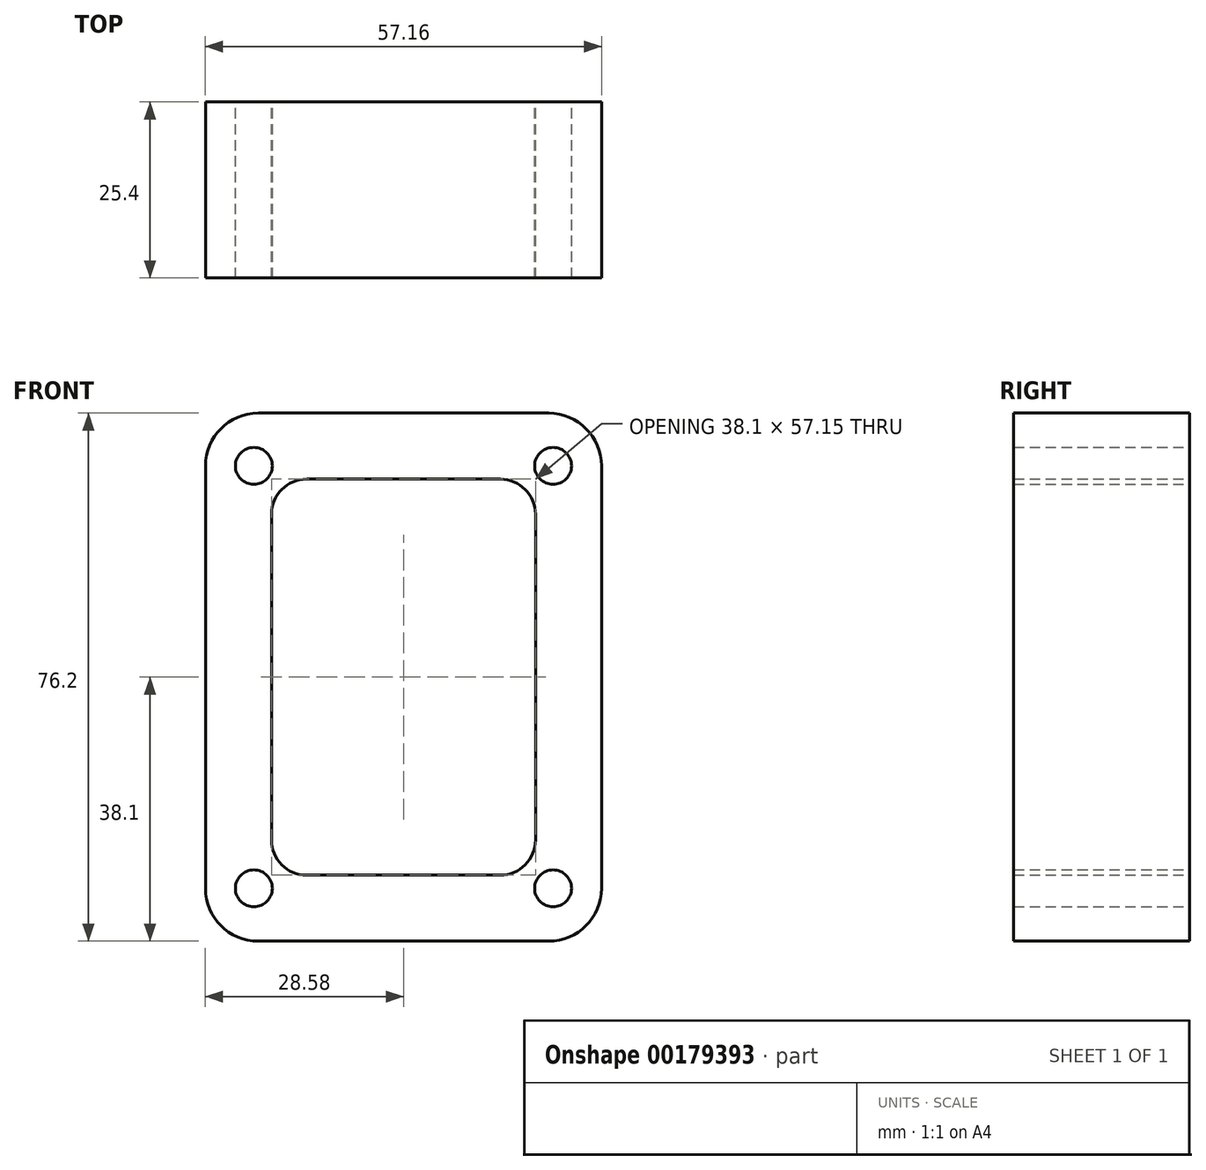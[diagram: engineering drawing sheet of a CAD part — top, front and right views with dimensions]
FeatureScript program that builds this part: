
annotation { "Feature Type Name" : "Feature", "Feature Type Description" : "" }
export const myFeature = defineFeature(function(context is Context, id is Id, definition is map)
    precondition{}
    {
        {
            var Q0;
            Q0=qCreatedBy(makeId("Front.planeOp"),FACE);
            var sketch = newSketch(context, id + "F0", { "sketchPlane" : qUnion([Q0])});
            skLineSegment(sketch, "E0.bottom", {"start": v(-13.97, 28.58) * mm, "end": v(13.97, 28.58) * mm});
            skLineSegment(sketch, "E0.top", {"start": v(-13.97, -28.58) * mm, "end": v(13.97, -28.58) * mm});
            skLineSegment(sketch, "E0.left", {"start": v(-19.05, 23.5) * mm, "end": v(-19.05, -23.5) * mm});
            skLineSegment(sketch, "E0.right", {"start": v(19.05, 23.5) * mm, "end": v(19.05, -23.5) * mm});
            skLineSegment(sketch, "E1.bottom", {"start": v(-20.95, 38.1) * mm, "end": v(20.96, 38.1) * mm});
            skLineSegment(sketch, "E1.top", {"start": v(-20.96, -38.1) * mm, "end": v(20.96, -38.1) * mm});
            skLineSegment(sketch, "E1.left", {"start": v(-28.58, 30.48) * mm, "end": v(-28.58, -30.48) * mm});
            skLineSegment(sketch, "E1.right", {"start": v(28.57, 30.48) * mm, "end": v(28.58, -30.48) * mm});
            skCircle(sketch, "E2", {"center": v(21.6, -30.48) * mm, "radius": 2.67 * mm});
            skCircle(sketch, "E3", {"center": v(21.59, 30.48) * mm, "radius": 2.67 * mm});
            skCircle(sketch, "E4", {"center": v(-21.6, 30.48) * mm, "radius": 2.67 * mm});
            skCircle(sketch, "E5", {"center": v(-21.59, -30.48) * mm, "radius": 2.67 * mm});
            skPoint(sketch, "E6.visualSharp", {"position": v(28.58, -38.1) * mm});
            skArc(sketch, "E6.filletArc", {"start": v(20.96, -38.1) * mm, "mid": v(26.34, -35.87) * mm, "end": v(28.58, -30.48) * mm});
            skPoint(sketch, "E7.visualSharp", {"position": v(-28.58, -38.1) * mm});
            skArc(sketch, "E7.filletArc", {"start": v(-28.58, -30.48) * mm, "mid": v(-26.34, -35.87) * mm, "end": v(-20.96, -38.1) * mm});
            skPoint(sketch, "E8.visualSharp", {"position": v(-28.57, 38.1) * mm});
            skArc(sketch, "E8.filletArc", {"start": v(-20.95, 38.1) * mm, "mid": v(-26.34, 35.87) * mm, "end": v(-28.57, 30.48) * mm});
            skPoint(sketch, "E9.visualSharp", {"position": v(28.57, 38.1) * mm});
            skArc(sketch, "E9.filletArc", {"start": v(28.58, 30.48) * mm, "mid": v(26.34, 35.87) * mm, "end": v(20.96, 38.1) * mm});
            skPoint(sketch, "E10.visualSharp", {"position": v(19.05, -28.58) * mm});
            skArc(sketch, "E10.filletArc", {"start": v(13.97, -28.58) * mm, "mid": v(17.56, -27.09) * mm, "end": v(19.05, -23.5) * mm});
            skPoint(sketch, "E11.visualSharp", {"position": v(19.05, 28.58) * mm});
            skArc(sketch, "E11.filletArc", {"start": v(19.05, 23.5) * mm, "mid": v(17.56, 27.09) * mm, "end": v(13.97, 28.58) * mm});
            skPoint(sketch, "E12.visualSharp", {"position": v(-19.05, 28.58) * mm});
            skArc(sketch, "E12.filletArc", {"start": v(-13.97, 28.58) * mm, "mid": v(-17.56, 27.09) * mm, "end": v(-19.05, 23.5) * mm});
            skPoint(sketch, "E13.visualSharp", {"position": v(-19.05, -28.58) * mm});
            skArc(sketch, "E13.filletArc", {"start": v(-19.05, -23.5) * mm, "mid": v(-17.56, -27.09) * mm, "end": v(-13.97, -28.58) * mm});
            skLineSegment(sketch, "E14.bottom", {"start": v(21.59, 30.48) * mm, "end": v(-21.6, 30.48) * mm, "construction": true});
            skLineSegment(sketch, "E14.top", {"start": v(21.6, -30.48) * mm, "end": v(-21.59, -30.48) * mm, "construction": true});
            skLineSegment(sketch, "E14.left", {"start": v(21.59, 30.48) * mm, "end": v(21.6, -30.48) * mm, "construction": true});
            skLineSegment(sketch, "E14.right", {"start": v(-21.6, 30.48) * mm, "end": v(-21.59, -30.48) * mm, "construction": true});
            skSolve(sketch);
        }
        {
            var Q0;
            Q0=makeQuery(id+"F0.imprint","IMPRINT",FACE,{"disambiguationData":[TD([[makeQuery(id+"F0.imprint","IMPRINT",EDGE,{"derivedFrom":sQuery(id+"F0.wireOp",EDGE,"E0.bottom")}),1.0]])]});
            extrude(context, id + "F1", {"entities" : qUnion([Q0]), "depth" : 25.4 * mm});
        }
    });
